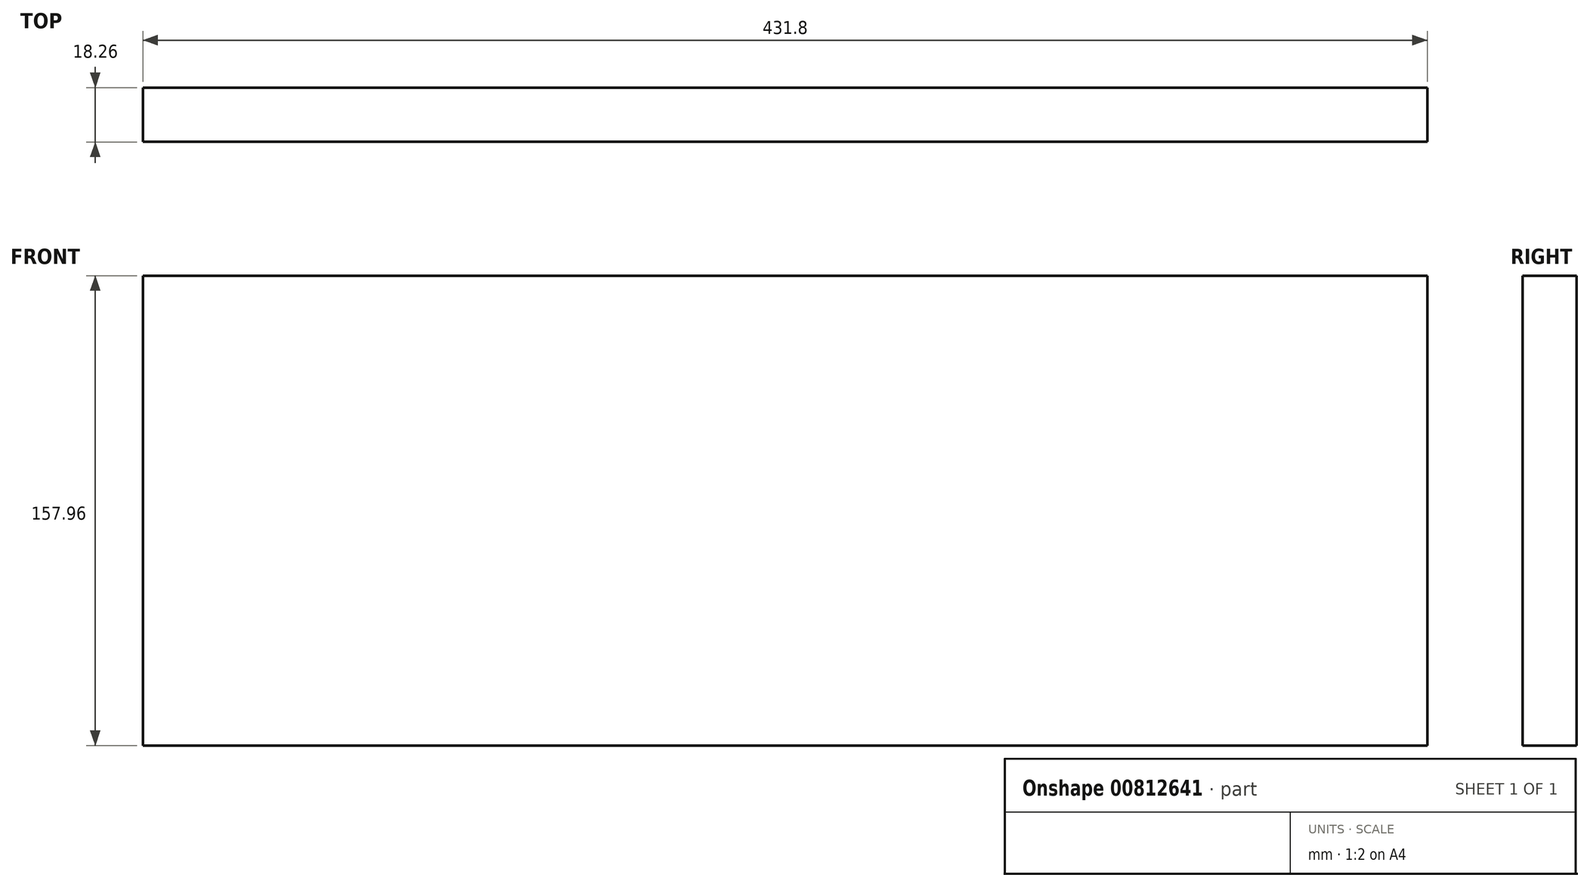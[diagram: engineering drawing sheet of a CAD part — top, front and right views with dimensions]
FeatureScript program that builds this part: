
annotation { "Feature Type Name" : "Feature", "Feature Type Description" : "" }
export const myFeature = defineFeature(function(context is Context, id is Id, definition is map)
    precondition{}
    {
        {
            var Q0;
            Q0=qCreatedBy(makeId("Front.planeOp"),FACE);
            var sketch = newSketch(context, id + "F0", { "sketchPlane" : qUnion([Q0])});
            skLineSegment(sketch, "E0.bottom", {"start": v(-215.9, 78.98) * mm, "end": v(215.9, 78.98) * mm});
            skLineSegment(sketch, "E0.top", {"start": v(-215.9, -78.98) * mm, "end": v(215.9, -78.98) * mm});
            skLineSegment(sketch, "E0.left", {"start": v(-215.9, 78.98) * mm, "end": v(-215.9, -78.98) * mm});
            skLineSegment(sketch, "E0.right", {"start": v(215.9, 78.98) * mm, "end": v(215.9, -78.98) * mm});
            skPoint(sketch, "E0.middle", {"position": v(0, 0) * mm});
            skSolve(sketch);
        }
        {
            var Q0;
            Q0=qSketchRegion(id+"F0",true);
            extrude(context, id + "F1", {"entities" : qUnion([Q0]), "depth" : 18.26 * mm, "offsetDistance" : 25.4 * mm});
        }
    });
